# Revit family: VNRBS
name_source: partatom
category: Mechanical Equipment
revit_build: Autodesk Revit 2017 (Build: 20181011_1645(x64)
units: mm (PartAtom-declared; Revit-internal decimal feet)

## family parameters
Always vertical = Yes
Cut with Voids When Loaded = No
OmniClass Number = 23.40.40.11.17
OmniClass Title = Refrigerated Cases
Part Type = Normal
Room Calculation Point = No
Round Connector Dimension = Use Diameter
Shared = Yes
Work Plane-Based = Yes

## types (4) — shared parameters
24" Shelf = Yes
Application Discipline = Meat
BTUH Conventional = 810
BTUH Parallel = 777
DATE = 03-18-2015
DISCHARGE AIR TEMP = 0 °F
Default Elevation = 48"
Defrosts Per Day_2 = 2
Description = VNRB
Discharge Air (°F) = 33° F
Discharge Air Velocity (FPM) = 360 (FPM)
EQUIPMENT DESCRIPTION = VNRB
EQUIPMENT MARK = VNRBS
EVAP TEMPERATURE = 0 °F
Evaporator (°F) = 28° F
GE Gen6 Amps = 1 A
GE Gen6 Watts = 79 W
GLASS = Glass
GLASS CLAMP = <By Category>
Height = 67 7/8"
High Efficiency Amps = 1 A
High Efficiency Watts = 78 W
Infinity 90 Amps = 2 A
Infinity 90 Watts = 236 W
Item Description = VNRB
Keynote = VNRB
LEDStixx Amps = 1 A
LEDStixx Watts = 118 W
Legend Number = VNRB
Length of Cases = 150"
Manufacturer = HILL PHOENIX
Model = VNRB
Number of Fans per Case = 3
PAINTED METAL UPPER SHELF = <By Category>
PVC PIPE = <By Category>
Pro24 35K Hi Output Amps = 1 A
Pro24 35K Hi Output Watts = 120 W
REFRIGERATION PIPING = <By Category>
STAINLESS STEEL = GALVANIZED STEEL
Size of Door = 30"
Superheat Set Point @ Bulb (°F) = 6-8° F
TIMED OFF DEFROST FAIL-SAFE (Min) = 30
TIMED OFF DEFROST TERMINATION TEMP = 42 °F
TIMED-OFF DEFROST FAIL SAFE (MIN) = 30
TIMED-OFF DEFROST TERMINATION TEMP = 42 °F
Timed-Off Defrost Fail-Safe (Min) = 30 (Min)
Timed-Off Defrost Termination Temp_2 = 42° F
Trim colour = <By Category>
Type of Door Swing = A-Swing
URL = http://www.hillphoenix.com
VISTA C - WATTS = 0 W
Vista Amps = 2 A
Vista Watts = 293 W
Vista-C Amps = 0 A
Vista-C Watts = 0 W
Vista-C/60 Amps = 2 A
Vista-C/60 Watts = 293 W
Vista-E Amps = 0 A
Vista-E Watts = 0 W
Width = 37 1/8"
pannel colour = <By Category>
vista c watts = 0 W
zero-valued in all types: Actual Weight, DEFROSTS PER DAY, Load Mbh, NUMBER FOR ELECTRICAL DATA, NUMBER FOR GUIDLINES AND CONTROL ORGANIZATION, Number of Fans

## per-type parameters (varying)
| type | CENTER LINE | Length | No. OF DOORS | REF PLANE LEFT RIGHT |
| 5-Door | 75" | 150" | 5 | 75" |
| 4-Door | 60" | 120" | 4 | 60" |
| 3-Door | 45" | 90" | 3 | 45" |
| 2-Door | 30" | 60" | 2 | 30" |

## geometry (parser evidence)
native form markers: Blend x4, Sweep x32
no freeform markers — native parametric forms only
